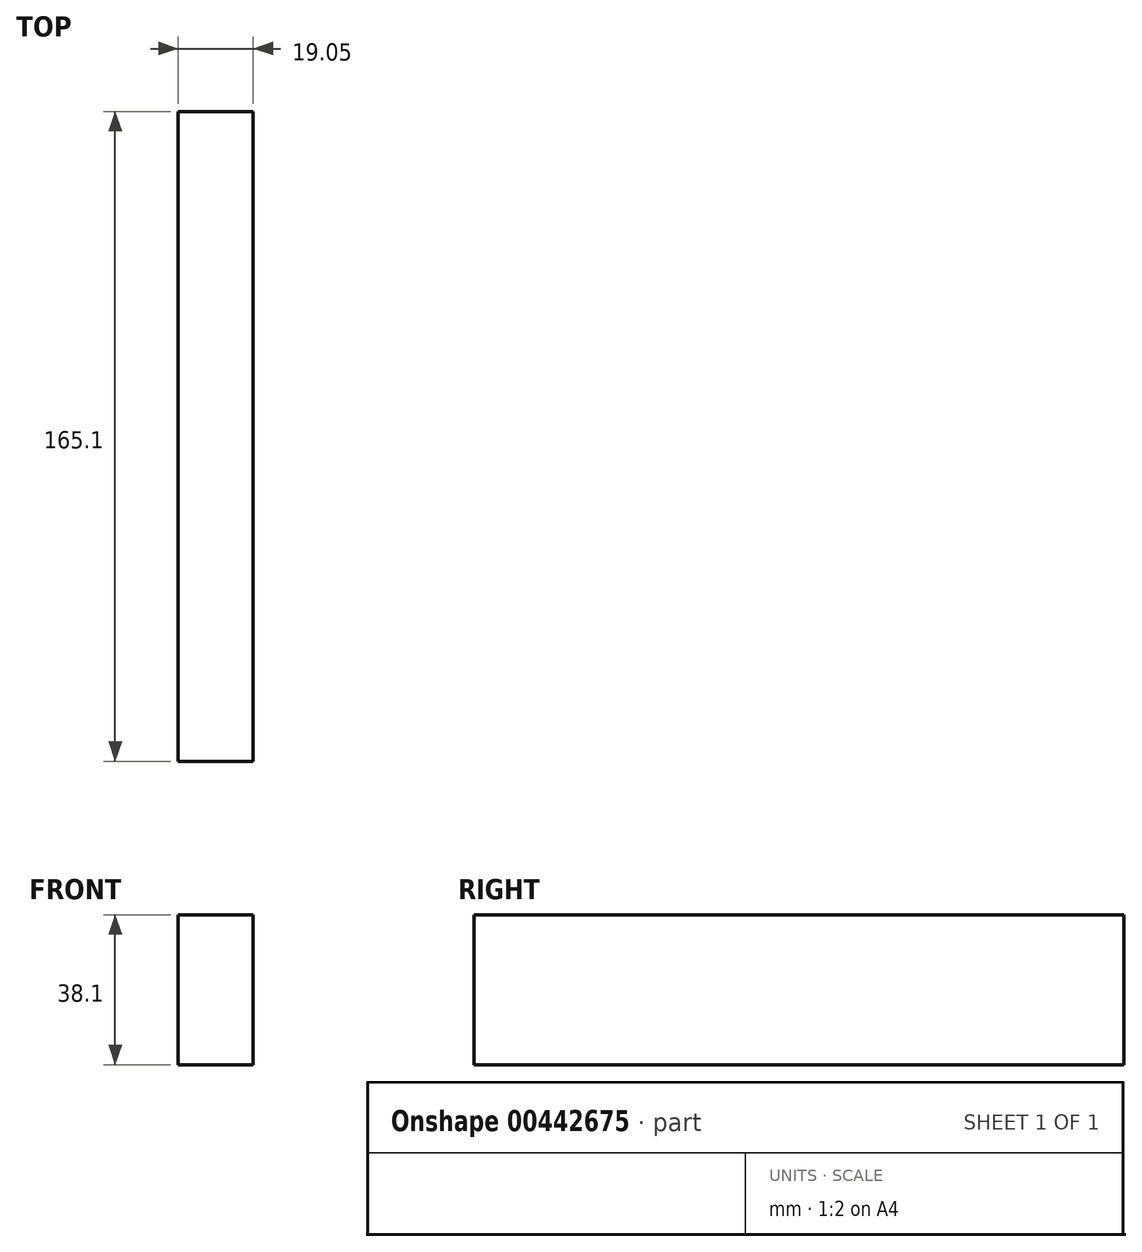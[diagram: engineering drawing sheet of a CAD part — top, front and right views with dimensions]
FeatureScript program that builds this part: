
annotation { "Feature Type Name" : "Feature", "Feature Type Description" : "" }
export const myFeature = defineFeature(function(context is Context, id is Id, definition is map)
    precondition{}
    {
        {
            var Q0;
            Q0=qCreatedBy(makeId("Right.planeOp"),FACE);
            var sketch = newSketch(context, id + "F0", { "sketchPlane" : qUnion([Q0])});
            skLineSegment(sketch, "E0.bottom", {"start": v(0, 0) * mm, "end": v(-165.1, 0) * mm});
            skLineSegment(sketch, "E0.top", {"start": v(0, 38.1) * mm, "end": v(-165.1, 38.1) * mm});
            skLineSegment(sketch, "E0.left", {"start": v(0, 0) * mm, "end": v(0, 38.1) * mm});
            skLineSegment(sketch, "E0.right", {"start": v(-165.1, 0) * mm, "end": v(-165.1, 38.1) * mm});
            skSolve(sketch);
        }
        {
            var Q0;
            Q0 = qSketchRegion(id + "F0", true);
            extrude(context, id + "F1", {"entities" : qUnion([Q0]), "depth" : 19.05 * mm});
        }
    });
